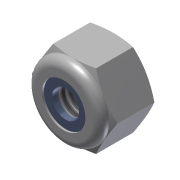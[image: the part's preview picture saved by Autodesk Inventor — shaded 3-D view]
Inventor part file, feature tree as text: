
AUTODESK INVENTOR PART (.ipt)
format: ipt  version: 2013 (Build 170138000, 138)  size: 182,784 bytes
history: native  units: in
note: dims shown in document units (in); Inventor stores cm internally (conversion verified against a paired STEP export)
features: sketch x5, extrude x2, revolve x2, projected_geometry x2, hole x1
ambient origin geometry x8: Origin, YZ Plane, XZ Plane, XY Plane, X Axis, Y Axis, Z Axis, Center Point
bodies: Solid1 (feature_tree)
feature tree (12):
  extrude  "Extrusion1"  Depth=0.195in TaperAngle=0.0deg
  revolve  "Revolution1"  [1 undecoded]
  revolve  "Revolution2"  Angle=90.0deg
  hole  "Hole1"  [1 undecoded]
  extrude  "Extrusion2"  Depth=0.027in
  sketch  "Sketch1"  dims[d0=0.3438in d1=0.195in d2=0.0in]
  sketch  "Sketch2"  dims[d5=0.039in d6=0.039in]
  sketch  "Sketch3"  dims[d7=0.133in d8=90.0deg]
  sketch  "Sketch4"  dims[d9=0.027in d10=0.012in]
  sketch  "Sketch5"  dims[d11=0.012in d12=0.027in d13=90.0deg d14=0.13in d15=0.75in d16=0.201in d17=0.009in d18=0.5635in d19=1.0in d20=0.8108in d21=0.125in d24=0.027in d25=0.0in]
  projected_geometry  "Project Cut Edges1"
  projected_geometry  "Project Cut Edges2"
note: 2 required parameter values undecoded (feature->parameter linkage not recoverable at this tier; creation-order binding heuristic only, values carry confidence <= 0.55)